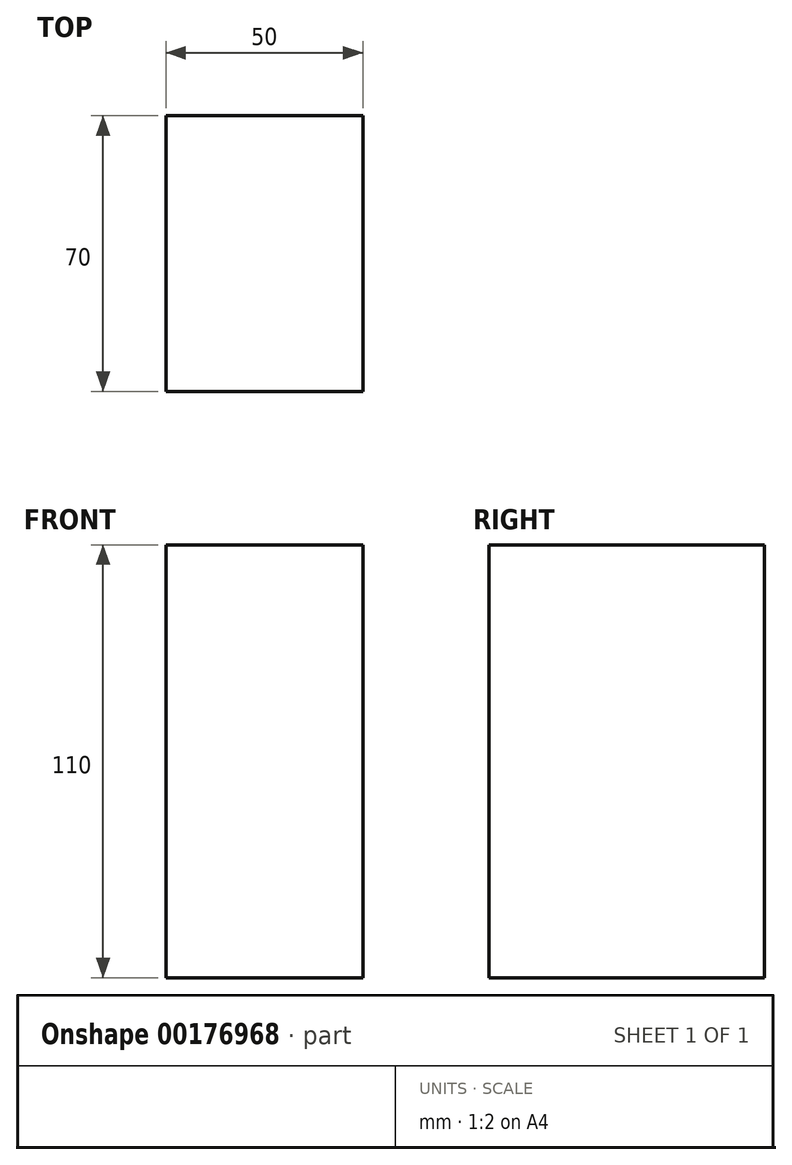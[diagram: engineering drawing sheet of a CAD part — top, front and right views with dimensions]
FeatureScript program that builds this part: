
annotation { "Feature Type Name" : "Feature", "Feature Type Description" : "" }
export const myFeature = defineFeature(function(context is Context, id is Id, definition is map)
    precondition{}
    {
        {
            assignVariable(context, id + "F0", {"name" : "probeHeight", "anyValue" : 110});
        }
        {
            var Q0;
            Q0=qCreatedBy(makeId("Top.planeOp"),FACE);
            var sketch = newSketch(context, id + "F1", { "sketchPlane" : qUnion([Q0])});
            skLineSegment(sketch, "E0.bottom", {"start": v(-25, 35) * mm, "end": v(25, 35) * mm});
            skLineSegment(sketch, "E0.top", {"start": v(-25, -35) * mm, "end": v(25, -35) * mm});
            skLineSegment(sketch, "E0.left", {"start": v(-25, 35) * mm, "end": v(-25, -35) * mm});
            skLineSegment(sketch, "E0.right", {"start": v(25, 35) * mm, "end": v(25, -35) * mm});
            skPoint(sketch, "E0.middle", {"position": v(0, 0) * mm});
            skSolve(sketch);
        }
        {
            var Q0;
            Q0=qSketchRegion(id+"F1",true);
            extrude(context, id + "F2", {"entities" : qUnion([Q0]), "depth" : (getVariable(context, 'probeHeight')) * mm});
        }
    });
